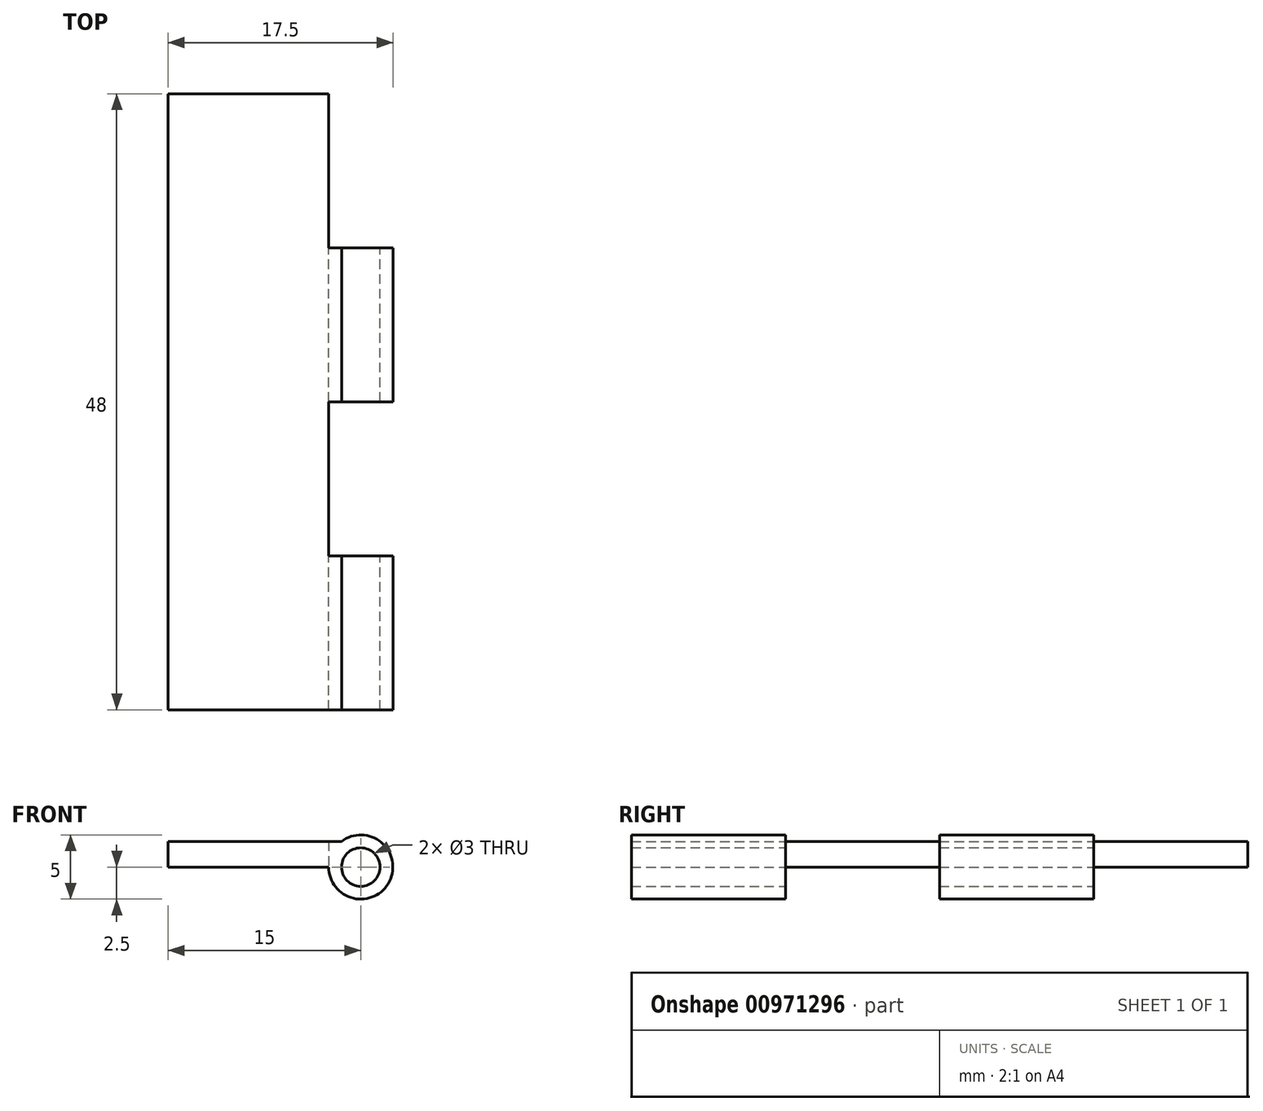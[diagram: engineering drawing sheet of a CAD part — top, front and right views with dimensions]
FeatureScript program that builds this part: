
annotation { "Feature Type Name" : "Feature", "Feature Type Description" : "" }
export const myFeature = defineFeature(function(context is Context, id is Id, definition is map)
    precondition{}
    {
        {
            var Q0;
            Q0=qCreatedBy(makeId("Front.planeOp"),FACE);
            var sketch = newSketch(context, id + "F0", { "sketchPlane" : qUnion([Q0])});
            skLineSegment(sketch, "E0.bottom", {"start": v(-15, 2) * mm, "end": v(-1.5, 2) * mm});
            skLineSegment(sketch, "E0.top", {"start": v(-15, 0) * mm, "end": v(-2.5, 0) * mm});
            skLineSegment(sketch, "E0.left", {"start": v(-15, 2) * mm, "end": v(-15, 0) * mm});
            skArc(sketch, "E1", {"start": v(-2.5, 0) * mm, "mid": v(2.24, -1.12) * mm, "end": v(-1.5, 2) * mm});
            skCircle(sketch, "E2", {"center": v(0, 0) * mm, "radius": 1.5 * mm});
            skSolve(sketch);
        }
        {
            var Q0;
            Q0=makeQuery(id+"F0.imprint","IMPRINT",FACE,{"disambiguationData":[TD([[makeQuery(id+"F0.imprint","IMPRINT",EDGE,{"derivedFrom":sQuery(id+"F0.wireOp",EDGE,"E0.bottom")}),-1.0]])]});
            extrude(context, id + "F1", {"entities" : qUnion([Q0]), "depth" : 48 * mm, "offsetDistance" : 25 * mm});
        }
        {
            var Q0;
            Q0=makeQuery(id+"F1.opExtrude","SWEPT_FACE",FACE,{"disambiguationData":[OSD([sQuery(id+"F0.wireOp",EDGE,"E0.top")])]});
            var sketch = newSketch(context, id + "F2", { "sketchPlane" : qUnion([Q0])});
            skLineSegment(sketch, "E3.bottom", {"start": v(-2.5, 0) * mm, "end": v(2.5, 0) * mm});
            skLineSegment(sketch, "E3.top", {"start": v(-2.5, 12) * mm, "end": v(2.5, 12) * mm});
            skLineSegment(sketch, "E3.left", {"start": v(-2.5, 0) * mm, "end": v(-2.5, 12) * mm});
            skLineSegment(sketch, "E3.right", {"start": v(2.5, 0) * mm, "end": v(2.5, 12) * mm});
            skLineSegment(sketch, "E4.0.1.0", {"start": v(2.5, 24) * mm, "end": v(2.5, 36) * mm});
            skLineSegment(sketch, "E4.0.1.1", {"start": v(-2.5, 36) * mm, "end": v(2.5, 36) * mm});
            skLineSegment(sketch, "E4.0.1.2", {"start": v(-2.5, 24) * mm, "end": v(-2.5, 36) * mm});
            skLineSegment(sketch, "E4.0.1.3", {"start": v(-2.5, 24) * mm, "end": v(2.5, 24) * mm});
            skLineSegment(sketch, "E4.direction1", {"start": v(-2.5, 0) * mm, "end": v(22.5, 0) * mm, "construction": true});
            skLineSegment(sketch, "E4.direction2", {"start": v(-2.5, 0) * mm, "end": v(-2.5, 24) * mm, "construction": true});
            skSolve(sketch);
        }
        {
            var Q0;
            Q0 = qSketchRegion(id + "F2", true);
            extrude(context, id + "F3", {"entities" : qUnion([Q0]), "operationType" : NewBodyOperationType.REMOVE, "oppositeDirection" : true, "depth" : 10 * mm, "offsetDistance" : 25 * mm, "symmetric" : true});
        }
    });
